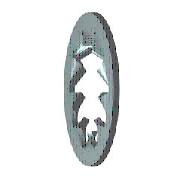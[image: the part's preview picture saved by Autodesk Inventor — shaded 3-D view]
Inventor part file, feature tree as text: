
AUTODESK INVENTOR PART (.ipt)
format: ipt  version: 2015 (Build 190159000, 159)  size: 163,840 bytes
history: native  units: mm (DEFAULTED — no unit token found)
features: sketch x2, extrude x1, pattern_circular x1, plane x1
ambient origin geometry x7: Origin, YZ Plane, XY Plane, X Axis, Y Axis, Z Axis, Center Point
bodies: Solid1 (feature_tree), Body (feature_tree)
feature tree (5):
  extrude  "Cut"  Depth=4.953mm
  pattern_circular  "Cuts"  [2 undecoded]
  plane  "Work Plane1"
  sketch  "Sketch1"  dims[d0=9.6774mm d1=4.953mm]
  sketch  "Sketch2"  dims[d2=0.6096mm d3=0.0mm d4=7.3152mm d5=1.963495mm d6=0.6096mm d7=0.0mm d8=0.14859mm d9=80.0mm d11=360.0deg d12=0.0mm d13=0.0mm d18=0.0mm d19=0.0mm]
note: 2 required parameter values undecoded (feature->parameter linkage not recoverable at this tier; creation-order binding heuristic only, values carry confidence <= 0.55)
